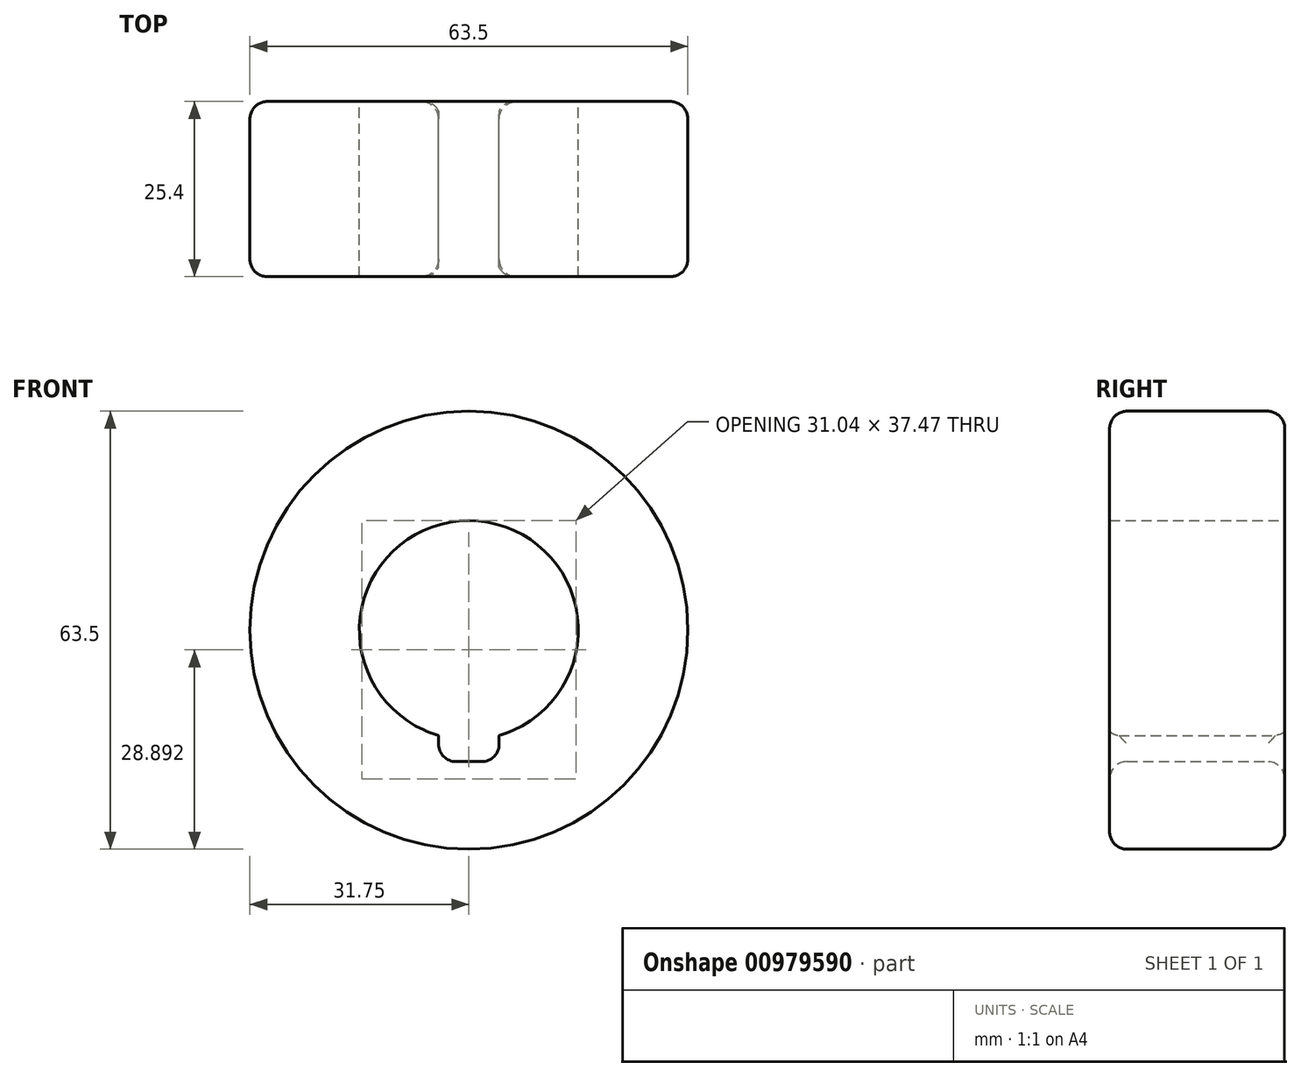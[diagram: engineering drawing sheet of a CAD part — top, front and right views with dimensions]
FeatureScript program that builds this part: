
annotation { "Feature Type Name" : "Feature", "Feature Type Description" : "" }
export const myFeature = defineFeature(function(context is Context, id is Id, definition is map)
    precondition{}
    {
        {
            var Q0;
            Q0=qCreatedBy(makeId("Front.planeOp"),FACE);
            var sketch = newSketch(context, id + "F0", { "sketchPlane" : qUnion([Q0])});
            skCircle(sketch, "E0", {"center": v(0, 0) * mm, "radius": 15.88 * mm});
            skCircle(sketch, "E1", {"center": v(0, 0) * mm, "radius": 31.75 * mm});
            skLineSegment(sketch, "E2.bottom", {"start": v(-4.39, -19.05) * mm, "end": v(4.39, -19.05) * mm});
            skLineSegment(sketch, "E2.top", {"start": v(-4.39, -7.85) * mm, "end": v(4.39, -7.85) * mm});
            skLineSegment(sketch, "E2.left", {"start": v(-4.39, -19.05) * mm, "end": v(-4.39, -7.85) * mm});
            skLineSegment(sketch, "E2.right", {"start": v(4.39, -19.05) * mm, "end": v(4.39, -7.85) * mm});
            skPoint(sketch, "E2.middle", {"position": v(0, -13.45) * mm});
            skLineSegment(sketch, "E3", {"start": v(0, -13.45) * mm, "end": v(0, 0) * mm, "construction": true});
            skSolve(sketch);
        }
        {
            var Q0;
            Q0=makeQuery(id+"F0.imprint","IMPRINT",FACE,{"disambiguationData":[TD([[makeQuery(id+"F0.imprint","IMPRINT",EDGE,{"derivedFrom":sQuery(id+"F0.wireOp",EDGE,"E1")}),1.0]])]});
            extrude(context, id + "F1", {"entities" : qUnion([Q0]), "endBound" : BoundingType.SYMMETRIC, "depth" : 25.4 * mm, "offsetDistance" : 25.4 * mm});
        }
        {
            var Q0;
            Q0=makeQuery(id+"F1.opExtrude","CAP_EDGE",EDGE,{"disambiguationData":[OSD([sQuery(id+"F0.wireOp",EDGE,"E1")])],"isStart":false});
            var Q1;
            Q1=makeQuery(id+"F1.opExtrude","CAP_EDGE",EDGE,{"disambiguationData":[OSD([sQuery(id+"F0.wireOp",EDGE,"E1")])],"isStart":true});
            var Q2;
            Q2=makeQuery(id+"F1.opExtrude","SWEPT_FACE",FACE,{"disambiguationData":[OSD([sQuery(id+"F0.wireOp",EDGE,"E2.bottom")])]});
            fillet(context, id + "F2", {"entities" : qUnion([Q0, Q1, Q2]), "radius" : 2.54 * mm, "tangentPropagation" : true, "allowEdgeOverflow" : false});
        }
    });
